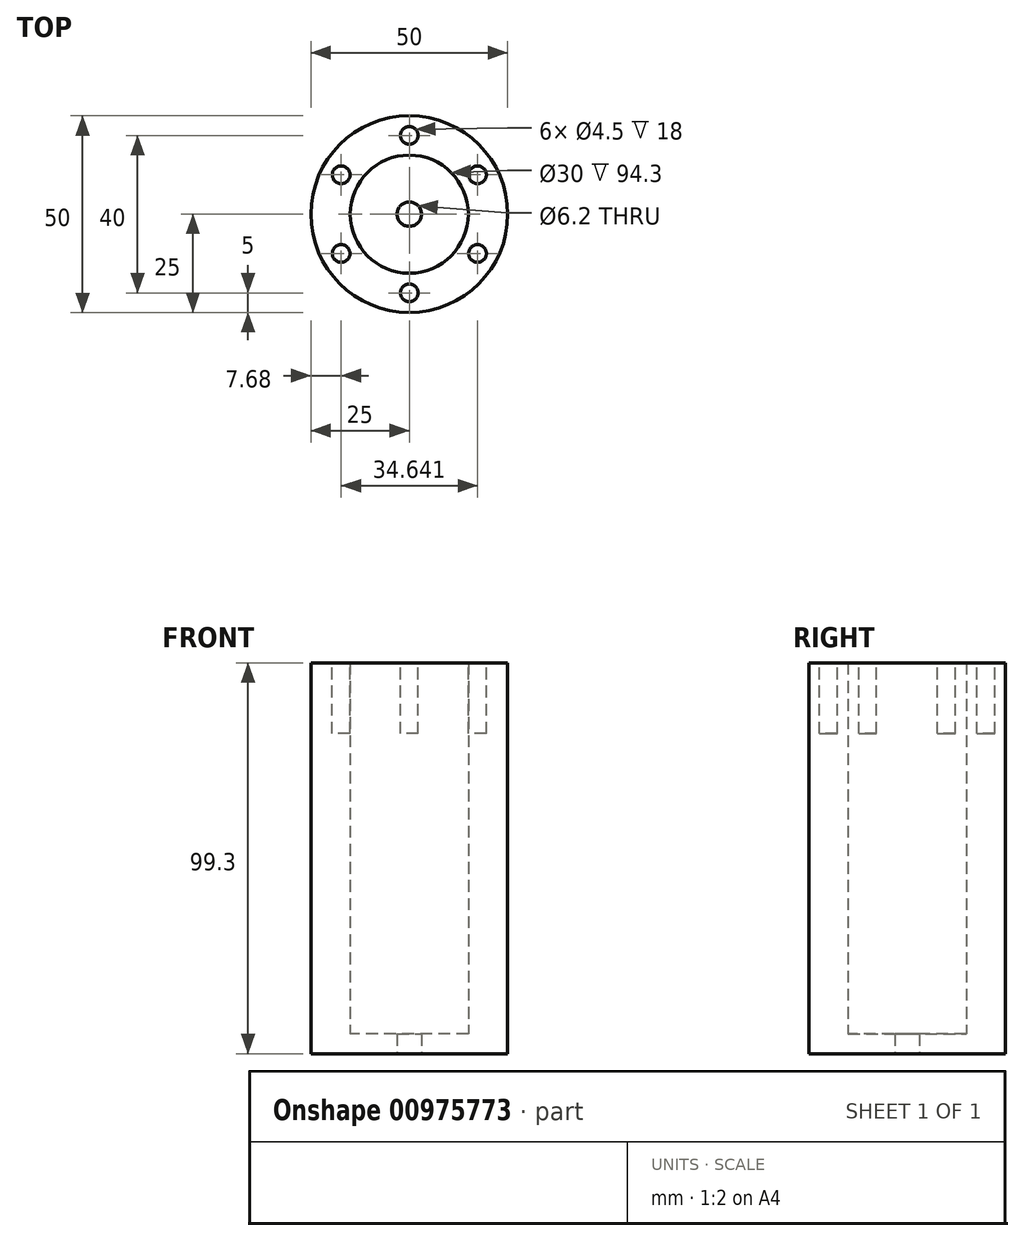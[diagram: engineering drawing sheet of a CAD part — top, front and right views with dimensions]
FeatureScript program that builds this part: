
annotation { "Feature Type Name" : "Feature", "Feature Type Description" : "" }
export const myFeature = defineFeature(function(context is Context, id is Id, definition is map)
    precondition{}
    {
        {
            var Q0;
            Q0=qCreatedBy(makeId("Top.planeOp"),FACE);
            var sketch = newSketch(context, id + "F0", { "sketchPlane" : qUnion([Q0])});
            skCircle(sketch, "E0", {"center": v(0, 0) * mm, "radius": 25 * mm});
            skCircle(sketch, "E1", {"center": v(0, 0) * mm, "radius": 15 * mm});
            skSolve(sketch);
        }
        {
            var Q0;
            Q0 = qSketchRegion(id + "F0", true);
            extrude(context, id + "F1", {"entities" : qUnion([Q0]), "depth" : 94.3 * mm, "offsetDistance" : 25 * mm});
        }
        {
            var Q0;
            Q0=makeQuery(id+"F1.opExtrude","CAP_FACE",FACE,{"disambiguationData":[OSD([sQuery(id+"F0.wireOp",EDGE,"E0"),sQuery(id+"F0.wireOp",EDGE,"E1")])],"isStart":false});
            var sketch = newSketch(context, id + "F2", { "sketchPlane" : qUnion([Q0])});
            skCircle(sketch, "E2", {"center": v(0, 20) * mm, "radius": 2.25 * mm});
            skCircle(sketch, "E3.1.0", {"center": v(-17.32, -10) * mm, "radius": 2.25 * mm});
            skCircle(sketch, "E3.2.0", {"center": v(17.32, -10) * mm, "radius": 2.25 * mm});
            skPoint(sketch, "E3.center", {"position": v(0, 0) * mm});
            skCircle(sketch, "E4", {"center": v(0, -20) * mm, "radius": 2.25 * mm});
            skCircle(sketch, "E5.1.0", {"center": v(17.32, 10) * mm, "radius": 2.25 * mm});
            skCircle(sketch, "E5.2.0", {"center": v(-17.32, 10) * mm, "radius": 2.25 * mm});
            skSolve(sketch);
        }
        {
            var Q0;
            Q0 = qSketchRegion(id + "F2", true);
            extrude(context, id + "F3", {"entities" : qUnion([Q0]), "operationType" : NewBodyOperationType.REMOVE, "oppositeDirection" : true, "depth" : 18 * mm, "offsetDistance" : 25 * mm});
        }
        {
            var Q0;
            Q0=makeQuery(id+"F1.opExtrude","CAP_FACE",FACE,{"disambiguationData":[OSD([sQuery(id+"F0.wireOp",EDGE,"E0"),sQuery(id+"F0.wireOp",EDGE,"E1")])],"isStart":true});
            var sketch = newSketch(context, id + "F4", { "sketchPlane" : qUnion([Q0])});
            skCircle(sketch, "E6", {"center": v(0, 0) * mm, "radius": 25 * mm});
            skSolve(sketch);
        }
        {
            var Q0;
            Q0 = qSketchRegion(id + "F4", true);
            extrude(context, id + "F5", {"entities" : qUnion([Q0]), "operationType" : NewBodyOperationType.ADD, "depth" : 5 * mm, "offsetDistance" : 25 * mm});
        }
        {
            var Q0;
            Q0=makeQuery(id+"F5.opExtrude","CAP_FACE",FACE,{"disambiguationData":[OSD([sQuery(id+"F4.wireOp",EDGE,"E6")])],"isStart":false});
            var sketch = newSketch(context, id + "F6", { "sketchPlane" : qUnion([Q0])});
            skCircle(sketch, "E7", {"center": v(0, 0) * mm, "radius": 3.1 * mm});
            skSolve(sketch);
        }
        {
            var Q0;
            Q0 = qSketchRegion(id + "F6", true);
            extrude(context, id + "F7", {"entities" : qUnion([Q0]), "operationType" : NewBodyOperationType.REMOVE, "oppositeDirection" : true, "depth" : 25 * mm, "offsetDistance" : 25 * mm});
        }
    });
